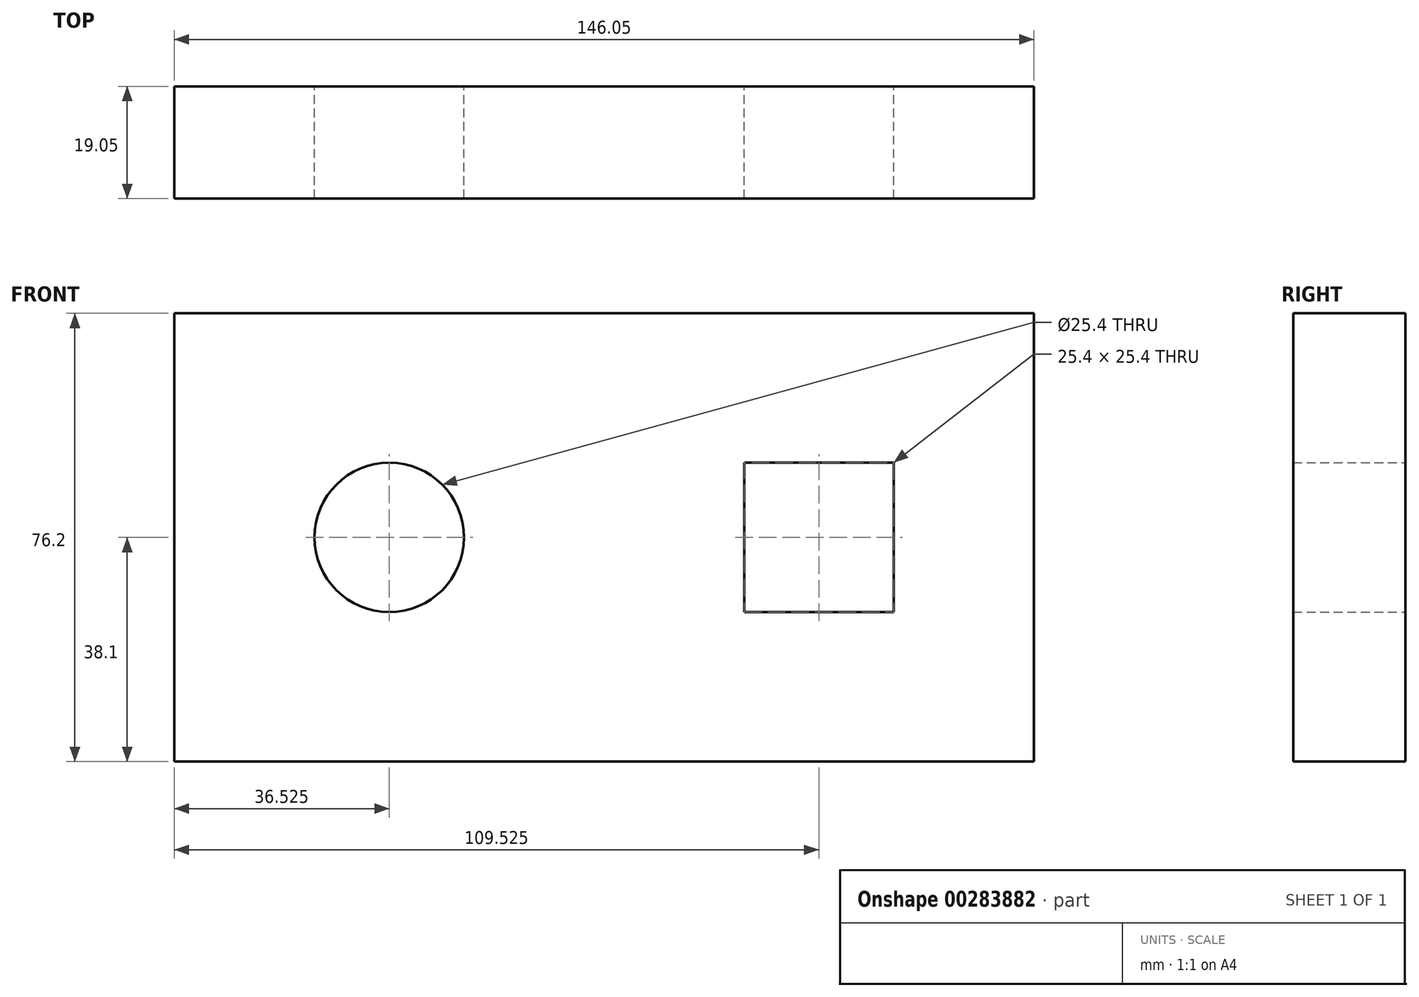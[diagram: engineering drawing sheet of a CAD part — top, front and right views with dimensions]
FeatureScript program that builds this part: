
annotation { "Feature Type Name" : "Feature", "Feature Type Description" : "" }
export const myFeature = defineFeature(function(context is Context, id is Id, definition is map)
    precondition{}
    {
        {
            var Q0;
            Q0=qCreatedBy(makeId("Front.planeOp"),FACE);
            var sketch = newSketch(context, id + "F0", { "sketchPlane" : qUnion([Q0])});
            skLineSegment(sketch, "E0", {"start": v(0, 0) * mm, "end": v(-146.05, 0) * mm});
            skLineSegment(sketch, "E1", {"start": v(-146.05, 0) * mm, "end": v(-146.05, 76.2) * mm});
            skLineSegment(sketch, "E2", {"start": v(-146.05, 76.2) * mm, "end": v(0, 76.2) * mm});
            skLineSegment(sketch, "E3", {"start": v(0, 76.2) * mm, "end": v(0, 0) * mm});
            skLineSegment(sketch, "E4", {"start": v(-49.23, 50.8) * mm, "end": v(-49.23, 25.4) * mm});
            skLineSegment(sketch, "E5", {"start": v(-49.23, 25.4) * mm, "end": v(-23.83, 25.4) * mm});
            skLineSegment(sketch, "E6", {"start": v(-23.83, 25.4) * mm, "end": v(-23.83, 50.8) * mm});
            skLineSegment(sketch, "E7", {"start": v(-23.83, 50.8) * mm, "end": v(-49.23, 50.8) * mm});
            skCircle(sketch, "E8", {"center": v(-109.52, 38.1) * mm, "radius": 12.7 * mm});
            skSolve(sketch);
        }
        {
            var Q0;
            Q0 = qSketchRegion(id + "F0", true);
            extrude(context, id + "F1", {"entities" : qUnion([Q0]), "depth" : 19.05 * mm});
        }
    });
